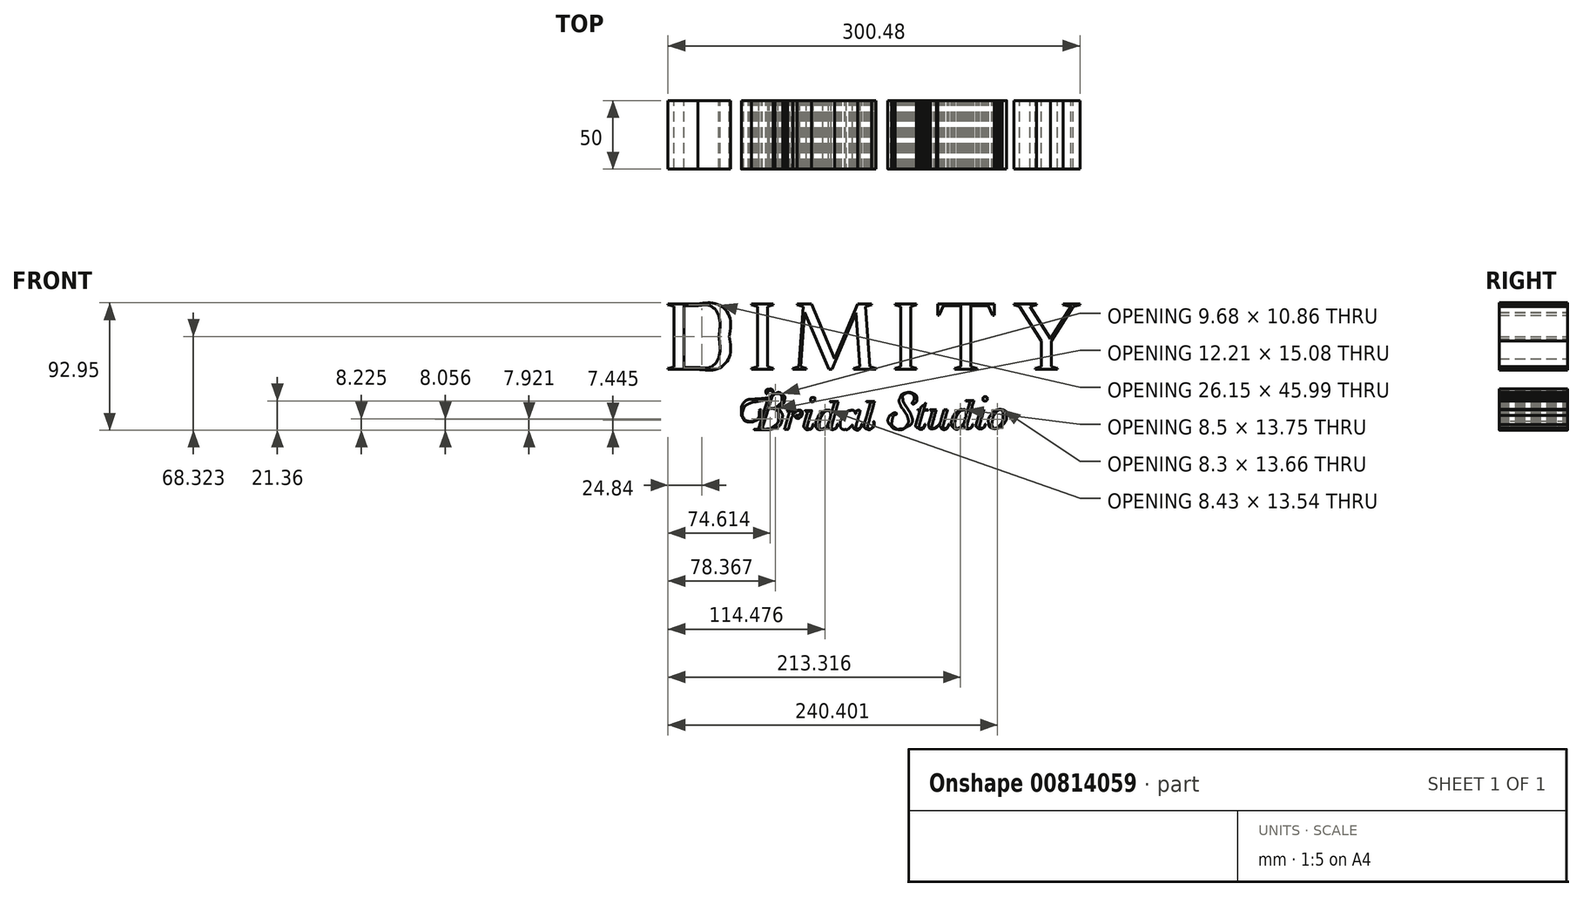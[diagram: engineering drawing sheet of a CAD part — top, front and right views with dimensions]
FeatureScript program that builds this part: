
annotation { "Feature Type Name" : "Feature", "Feature Type Description" : "" }
export const myFeature = defineFeature(function(context is Context, id is Id, definition is map)
    precondition{}
    {
        {
            var Q0;
            Q0=qCreatedBy(makeId("Front.planeOp"),FACE);
            var sketch = newSketch(context, id + "F0", { "sketchPlane" : qUnion([Q0])});
            skLineSegment(sketch, "E0", {"start": v(-150.24, 61.58) * mm, "end": v(-150.24, 60.97) * mm});
            skLineSegment(sketch, "E1", {"start": v(-150.24, 60.97) * mm, "end": v(-145.82, 59.95) * mm});
            skLineSegment(sketch, "E2", {"start": v(-145.82, 59.95) * mm, "end": v(-145.82, 15.6) * mm});
            skLineSegment(sketch, "E3", {"start": v(-145.82, 15.6) * mm, "end": v(-150.24, 14.5) * mm});
            skLineSegment(sketch, "E4", {"start": v(-150.24, 14.5) * mm, "end": v(-150.24, 13.96) * mm});
            skLineSegment(sketch, "E5", {"start": v(-150.24, 13.96) * mm, "end": v(-128.54, 13.96) * mm});
            skFitSpline(sketch, "E6", {"points": [v(-128.54, 13.96) * mm, v(-114.94, 13.96) * mm, v(-105.41, 22.8) * mm, v(-105.41, 37.77) * mm]});
            skFitSpline(sketch, "E7", {"points": [v(-105.41, 37.77) * mm, v(-105.41, 52.6) * mm, v(-114.94, 61.58) * mm, v(-128.54, 61.58) * mm]});
            skLineSegment(sketch, "E8", {"start": v(-128.54, 61.58) * mm, "end": v(-150.24, 61.58) * mm});
            skLineSegment(sketch, "E9", {"start": v(-138.48, 60.22) * mm, "end": v(-128.54, 60.22) * mm});
            skFitSpline(sketch, "E10", {"points": [v(-128.54, 60.22) * mm, v(-119.56, 60.22) * mm, v(-113.1, 52.74) * mm, v(-113.1, 37.7) * mm]});
            skFitSpline(sketch, "E11", {"points": [v(-113.1, 37.7) * mm, v(-113.1, 22.74) * mm, v(-119.56, 15.32) * mm, v(-128.54, 15.32) * mm]});
            skLineSegment(sketch, "E12", {"start": v(-128.54, 15.32) * mm, "end": v(-138.48, 15.32) * mm});
            skLineSegment(sketch, "E13", {"start": v(-138.48, 15.32) * mm, "end": v(-138.48, 60.22) * mm});
            skLineSegment(sketch, "E14", {"start": v(-89.22, 61.58) * mm, "end": v(-89.22, 60.9) * mm});
            skLineSegment(sketch, "E15", {"start": v(-89.22, 60.9) * mm, "end": v(-84.8, 59.6) * mm});
            skLineSegment(sketch, "E16", {"start": v(-84.8, 59.6) * mm, "end": v(-84.8, 15.93) * mm});
            skLineSegment(sketch, "E17", {"start": v(-84.8, 15.93) * mm, "end": v(-89.22, 14.64) * mm});
            skLineSegment(sketch, "E18", {"start": v(-89.22, 14.64) * mm, "end": v(-89.22, 13.96) * mm});
            skLineSegment(sketch, "E19", {"start": v(-89.22, 13.96) * mm, "end": v(-73.37, 13.96) * mm});
            skLineSegment(sketch, "E20", {"start": v(-73.37, 13.96) * mm, "end": v(-73.37, 14.64) * mm});
            skLineSegment(sketch, "E21", {"start": v(-73.37, 14.64) * mm, "end": v(-77.59, 15.93) * mm});
            skLineSegment(sketch, "E22", {"start": v(-77.59, 15.93) * mm, "end": v(-77.59, 59.6) * mm});
            skLineSegment(sketch, "E23", {"start": v(-77.59, 59.6) * mm, "end": v(-73.37, 60.9) * mm});
            skLineSegment(sketch, "E24", {"start": v(-73.37, 60.9) * mm, "end": v(-73.37, 61.58) * mm});
            skLineSegment(sketch, "E25", {"start": v(-73.37, 61.58) * mm, "end": v(-89.22, 61.58) * mm});
            skLineSegment(sketch, "E26", {"start": v(-56.1, 61.58) * mm, "end": v(-56.1, 60.9) * mm});
            skLineSegment(sketch, "E27", {"start": v(-56.1, 60.9) * mm, "end": v(-51.67, 59.6) * mm});
            skLineSegment(sketch, "E28", {"start": v(-51.67, 59.6) * mm, "end": v(-54.87, 15.8) * mm});
            skLineSegment(sketch, "E29", {"start": v(-54.87, 15.8) * mm, "end": v(-59.29, 14.5) * mm});
            skLineSegment(sketch, "E30", {"start": v(-59.29, 14.5) * mm, "end": v(-59.29, 13.96) * mm});
            skLineSegment(sketch, "E31", {"start": v(-59.29, 13.96) * mm, "end": v(-49.29, 13.96) * mm});
            skLineSegment(sketch, "E32", {"start": v(-49.29, 13.96) * mm, "end": v(-49.29, 14.5) * mm});
            skLineSegment(sketch, "E33", {"start": v(-49.29, 14.5) * mm, "end": v(-53.44, 15.8) * mm});
            skLineSegment(sketch, "E34", {"start": v(-53.44, 15.8) * mm, "end": v(-50.51, 55.4) * mm});
            skLineSegment(sketch, "E35", {"start": v(-50.51, 55.4) * mm, "end": v(-32.76, 13.96) * mm});
            skLineSegment(sketch, "E36", {"start": v(-32.76, 13.96) * mm, "end": v(-30.51, 13.96) * mm});
            skLineSegment(sketch, "E37", {"start": v(-30.51, 13.96) * mm, "end": v(-13.03, 55.32) * mm});
            skLineSegment(sketch, "E38", {"start": v(-13.03, 55.32) * mm, "end": v(-10.17, 15.93) * mm});
            skLineSegment(sketch, "E39", {"start": v(-10.17, 15.93) * mm, "end": v(-14.6, 14.64) * mm});
            skLineSegment(sketch, "E40", {"start": v(-14.6, 14.64) * mm, "end": v(-14.6, 13.96) * mm});
            skLineSegment(sketch, "E41", {"start": v(-14.6, 13.96) * mm, "end": v(1.32, 13.96) * mm});
            skLineSegment(sketch, "E42", {"start": v(1.32, 13.96) * mm, "end": v(1.32, 14.64) * mm});
            skLineSegment(sketch, "E43", {"start": v(1.32, 14.64) * mm, "end": v(-2.9, 15.93) * mm});
            skLineSegment(sketch, "E44", {"start": v(-2.9, 15.93) * mm, "end": v(-6.02, 59.6) * mm});
            skLineSegment(sketch, "E45", {"start": v(-6.02, 59.6) * mm, "end": v(-1.8, 60.9) * mm});
            skLineSegment(sketch, "E46", {"start": v(-1.8, 60.9) * mm, "end": v(-1.8, 61.58) * mm});
            skLineSegment(sketch, "E47", {"start": v(-1.8, 61.58) * mm, "end": v(-11.8, 61.58) * mm});
            skLineSegment(sketch, "E48", {"start": v(-11.8, 61.58) * mm, "end": v(-28.68, 21.44) * mm});
            skLineSegment(sketch, "E49", {"start": v(-28.68, 21.44) * mm, "end": v(-45.68, 61.58) * mm});
            skLineSegment(sketch, "E50", {"start": v(-45.68, 61.58) * mm, "end": v(-56.1, 61.58) * mm});
            skLineSegment(sketch, "E51", {"start": v(15.27, 61.58) * mm, "end": v(15.27, 60.9) * mm});
            skLineSegment(sketch, "E52", {"start": v(15.27, 60.9) * mm, "end": v(19.7, 59.6) * mm});
            skLineSegment(sketch, "E53", {"start": v(19.7, 59.6) * mm, "end": v(19.7, 15.93) * mm});
            skLineSegment(sketch, "E54", {"start": v(19.7, 15.93) * mm, "end": v(15.27, 14.64) * mm});
            skLineSegment(sketch, "E55", {"start": v(15.27, 14.64) * mm, "end": v(15.27, 13.96) * mm});
            skLineSegment(sketch, "E56", {"start": v(15.27, 13.96) * mm, "end": v(31.12, 13.96) * mm});
            skLineSegment(sketch, "E57", {"start": v(31.12, 13.96) * mm, "end": v(31.12, 14.64) * mm});
            skLineSegment(sketch, "E58", {"start": v(31.12, 14.64) * mm, "end": v(26.9, 15.93) * mm});
            skLineSegment(sketch, "E59", {"start": v(26.9, 15.93) * mm, "end": v(26.9, 59.6) * mm});
            skLineSegment(sketch, "E60", {"start": v(26.9, 59.6) * mm, "end": v(31.12, 60.9) * mm});
            skLineSegment(sketch, "E61", {"start": v(31.12, 60.9) * mm, "end": v(31.12, 61.58) * mm});
            skLineSegment(sketch, "E62", {"start": v(31.12, 61.58) * mm, "end": v(15.27, 61.58) * mm});
            skLineSegment(sketch, "E63", {"start": v(46.5, 61.58) * mm, "end": v(46.5, 53.21) * mm});
            skLineSegment(sketch, "E64", {"start": v(46.5, 53.21) * mm, "end": v(47.59, 53.21) * mm});
            skLineSegment(sketch, "E65", {"start": v(47.59, 53.21) * mm, "end": v(50.79, 60.22) * mm});
            skLineSegment(sketch, "E66", {"start": v(50.79, 60.22) * mm, "end": v(63.44, 60.22) * mm});
            skLineSegment(sketch, "E67", {"start": v(63.44, 60.22) * mm, "end": v(63.44, 15.93) * mm});
            skLineSegment(sketch, "E68", {"start": v(63.44, 15.93) * mm, "end": v(59.02, 14.64) * mm});
            skLineSegment(sketch, "E69", {"start": v(59.02, 14.64) * mm, "end": v(59.02, 13.96) * mm});
            skLineSegment(sketch, "E70", {"start": v(59.02, 13.96) * mm, "end": v(75.2, 13.96) * mm});
            skLineSegment(sketch, "E71", {"start": v(75.2, 13.96) * mm, "end": v(75.2, 14.64) * mm});
            skLineSegment(sketch, "E72", {"start": v(75.2, 14.64) * mm, "end": v(70.79, 15.93) * mm});
            skLineSegment(sketch, "E73", {"start": v(70.79, 15.93) * mm, "end": v(70.79, 60.22) * mm});
            skLineSegment(sketch, "E74", {"start": v(70.79, 60.22) * mm, "end": v(83.5, 60.22) * mm});
            skLineSegment(sketch, "E75", {"start": v(83.5, 60.22) * mm, "end": v(86.64, 53.21) * mm});
            skLineSegment(sketch, "E76", {"start": v(86.64, 53.21) * mm, "end": v(87.8, 53.21) * mm});
            skLineSegment(sketch, "E77", {"start": v(87.8, 53.21) * mm, "end": v(87.8, 61.58) * mm});
            skLineSegment(sketch, "E78", {"start": v(87.8, 61.58) * mm, "end": v(46.5, 61.58) * mm});
            skLineSegment(sketch, "E79", {"start": v(102.08, 61.58) * mm, "end": v(102.08, 60.9) * mm});
            skLineSegment(sketch, "E80", {"start": v(102.08, 60.9) * mm, "end": v(106.3, 59.6) * mm});
            skLineSegment(sketch, "E81", {"start": v(106.3, 59.6) * mm, "end": v(122.22, 34.64) * mm});
            skLineSegment(sketch, "E82", {"start": v(122.22, 34.64) * mm, "end": v(122.22, 15.93) * mm});
            skLineSegment(sketch, "E83", {"start": v(122.22, 15.93) * mm, "end": v(117.8, 14.64) * mm});
            skLineSegment(sketch, "E84", {"start": v(117.8, 14.64) * mm, "end": v(117.8, 13.96) * mm});
            skLineSegment(sketch, "E85", {"start": v(117.8, 13.96) * mm, "end": v(133.71, 13.96) * mm});
            skLineSegment(sketch, "E86", {"start": v(133.71, 13.96) * mm, "end": v(133.71, 14.64) * mm});
            skLineSegment(sketch, "E87", {"start": v(133.71, 14.64) * mm, "end": v(129.5, 15.93) * mm});
            skLineSegment(sketch, "E88", {"start": v(129.5, 15.93) * mm, "end": v(129.5, 34.64) * mm});
            skLineSegment(sketch, "E89", {"start": v(129.5, 34.64) * mm, "end": v(145.41, 59.6) * mm});
            skLineSegment(sketch, "E90", {"start": v(145.41, 59.6) * mm, "end": v(150.24, 60.9) * mm});
            skLineSegment(sketch, "E91", {"start": v(150.24, 60.9) * mm, "end": v(150.24, 61.58) * mm});
            skLineSegment(sketch, "E92", {"start": v(150.24, 61.58) * mm, "end": v(138.14, 61.58) * mm});
            skLineSegment(sketch, "E93", {"start": v(138.14, 61.58) * mm, "end": v(138.14, 60.9) * mm});
            skLineSegment(sketch, "E94", {"start": v(138.14, 60.9) * mm, "end": v(143.85, 59.6) * mm});
            skLineSegment(sketch, "E95", {"start": v(143.85, 59.6) * mm, "end": v(128.82, 36.14) * mm});
            skLineSegment(sketch, "E96", {"start": v(128.82, 36.14) * mm, "end": v(113.99, 59.6) * mm});
            skLineSegment(sketch, "E97", {"start": v(113.99, 59.6) * mm, "end": v(118.48, 60.9) * mm});
            skLineSegment(sketch, "E98", {"start": v(118.48, 60.9) * mm, "end": v(118.48, 61.58) * mm});
            skLineSegment(sketch, "E99", {"start": v(118.48, 61.58) * mm, "end": v(102.08, 61.58) * mm});
            skFitSpline(sketch, "E100", {"points": [v(-76.4, -0.67) * mm, v(-76.52, -0.68) * mm, v(-76.64, -0.69) * mm, v(-76.77, -0.7) * mm]});
            skFitSpline(sketch, "E101", {"points": [v(-76.77, -0.7) * mm, v(-78.1, -0.88) * mm, v(-78.95, -2.12) * mm, v(-78.66, -3.42) * mm]});
            skFitSpline(sketch, "E102", {"points": [v(-78.66, -3.42) * mm, v(-78.58, -3.77) * mm, v(-78.42, -4.03) * mm, v(-78.01, -4.17) * mm]});
            skFitSpline(sketch, "E103", {"points": [v(-78.01, -4.17) * mm, v(-77.88, -3.84) * mm, v(-77.75, -3.53) * mm, v(-77.63, -3.23) * mm]});
            skFitSpline(sketch, "E104", {"points": [v(-77.63, -3.23) * mm, v(-77.3, -2.4) * mm, v(-76.7, -1.9) * mm, v(-75.86, -1.7) * mm]});
            skFitSpline(sketch, "E105", {"points": [v(-75.86, -1.7) * mm, v(-75.1, -1.5) * mm, v(-74.23, -1.76) * mm, v(-73.8, -2.9) * mm]});
            skFitSpline(sketch, "E106", {"points": [v(-73.8, -2.9) * mm, v(-73.64, -3.48) * mm, v(-73.71, -3.7) * mm, v(-73.8, -3.99) * mm]});
            skFitSpline(sketch, "E107", {"points": [v(-73.8, -3.99) * mm, v(-74.16, -4.85) * mm, v(-74.64, -5.5) * mm, v(-75.38, -5.97) * mm]});
            skFitSpline(sketch, "E108", {"points": [v(-75.38, -5.97) * mm, v(-76.37, -6.6) * mm, v(-77.46, -6.98) * mm, v(-78.6, -7.13) * mm]});
            skFitSpline(sketch, "E109", {"points": [v(-78.6, -7.13) * mm, v(-80.37, -7.36) * mm, v(-82.16, -7.53) * mm, v(-83.95, -7.6) * mm]});
            skFitSpline(sketch, "E110", {"points": [v(-83.95, -7.6) * mm, v(-85.37, -7.64) * mm, v(-86.76, -7.81) * mm, v(-88.16, -8) * mm]});
            skFitSpline(sketch, "E111", {"points": [v(-88.16, -8) * mm, v(-92.67, -8.6) * mm, v(-96.35, -12.56) * mm, v(-96.65, -16.82) * mm]});
            skFitSpline(sketch, "E112", {"points": [v(-96.65, -16.82) * mm, v(-96.76, -18.4) * mm, v(-96.57, -19.87) * mm, v(-95.83, -21.26) * mm]});
            skFitSpline(sketch, "E113", {"points": [v(-95.83, -21.26) * mm, v(-94.76, -23.27) * mm, v(-93.03, -24.27) * mm, v(-90.8, -24.44) * mm]});
            skFitSpline(sketch, "E114", {"points": [v(-90.8, -24.44) * mm, v(-89.36, -24.54) * mm, v(-87.99, -24.3) * mm, v(-86.66, -23.74) * mm]});
            skFitSpline(sketch, "E115", {"points": [v(-86.66, -23.74) * mm, v(-84.6, -22.87) * mm, v(-82.99, -21.52) * mm, v(-82.1, -19.41) * mm]});
            skFitSpline(sketch, "E116", {"points": [v(-82.1, -19.41) * mm, v(-81.75, -18.57) * mm, v(-81.63, -17.7) * mm, v(-81.92, -16.82) * mm]});
            skFitSpline(sketch, "E117", {"points": [v(-81.92, -16.82) * mm, v(-82.23, -15.91) * mm, v(-83.02, -15.66) * mm, v(-83.94, -16.22) * mm]});
            skFitSpline(sketch, "E118", {"points": [v(-83.94, -16.22) * mm, v(-83.56, -16.94) * mm, v(-83.62, -17.7) * mm, v(-83.68, -18.42) * mm]});
            skFitSpline(sketch, "E119", {"points": [v(-83.68, -18.42) * mm, v(-83.88, -20.82) * mm, v(-85.05, -22.56) * mm, v(-87.27, -23.54) * mm]});
            skFitSpline(sketch, "E120", {"points": [v(-87.27, -23.54) * mm, v(-88.7, -24.17) * mm, v(-90.18, -24.3) * mm, v(-91.7, -23.95) * mm]});
            skFitSpline(sketch, "E121", {"points": [v(-91.7, -23.95) * mm, v(-93.1, -23.63) * mm, v(-94.26, -22.9) * mm, v(-94.99, -21.61) * mm]});
            skFitSpline(sketch, "E122", {"points": [v(-94.99, -21.61) * mm, v(-95.98, -19.85) * mm, v(-96.04, -17.97) * mm, v(-95.36, -16.13) * mm]});
            skFitSpline(sketch, "E123", {"points": [v(-95.36, -16.13) * mm, v(-94.4, -13.55) * mm, v(-92.5, -11.84) * mm, v(-89.98, -10.77) * mm]});
            skFitSpline(sketch, "E124", {"points": [v(-89.98, -10.77) * mm, v(-88.26, -10.04) * mm, v(-86.4, -9.88) * mm, v(-84.6, -9.53) * mm]});
            skFitSpline(sketch, "E125", {"points": [v(-84.6, -9.53) * mm, v(-82.4, -9.1) * mm, v(-80.2, -8.66) * mm, v(-78.1, -7.82) * mm]});
            skFitSpline(sketch, "E126", {"points": [v(-78.1, -7.82) * mm, v(-77.9, -7.74) * mm, v(-77.67, -7.7) * mm, v(-77.37, -7.61) * mm]});
            skFitSpline(sketch, "E127", {"points": [v(-77.37, -7.61) * mm, v(-79.72, -15.08) * mm, v(-82.04, -22.44) * mm, v(-84.39, -29.86) * mm]});
            skFitSpline(sketch, "E128", {"points": [v(-84.39, -29.86) * mm, v(-84.9, -29.86) * mm, v(-85.4, -29.84) * mm, v(-85.9, -29.87) * mm]});
            skFitSpline(sketch, "E129", {"points": [v(-85.9, -29.87) * mm, v(-86.39, -29.9) * mm, v(-86.9, -29.73) * mm, v(-87.35, -30.07) * mm]});
            skFitSpline(sketch, "E130", {"points": [v(-87.35, -30.07) * mm, v(-87.1, -30.16) * mm, v(-86.84, -30.18) * mm, v(-86.58, -30.19) * mm]});
            skFitSpline(sketch, "E131", {"points": [v(-86.58, -30.19) * mm, v(-83.85, -30.19) * mm, v(-81.12, -30.18) * mm, v(-78.4, -30.19) * mm]});
            skFitSpline(sketch, "E132", {"points": [v(-78.4, -30.19) * mm, v(-77.22, -30.2) * mm, v(-76.05, -30.1) * mm, v(-74.92, -29.76) * mm]});
            skFitSpline(sketch, "E133", {"points": [v(-74.92, -29.76) * mm, v(-70.73, -28.54) * mm, v(-67.89, -25.98) * mm, v(-66.95, -21.6) * mm]});
            skFitSpline(sketch, "E134", {"points": [v(-66.95, -21.6) * mm, v(-66.64, -20.14) * mm, v(-66.88, -18.71) * mm, v(-67.65, -17.44) * mm]});
            skFitSpline(sketch, "E135", {"points": [v(-67.65, -17.44) * mm, v(-68.51, -16.03) * mm, v(-69.82, -15.18) * mm, v(-71.42, -14.78) * mm]});
            skFitSpline(sketch, "E136", {"points": [v(-71.42, -14.78) * mm, v(-71.73, -14.7) * mm, v(-72.03, -14.64) * mm, v(-72.33, -14.57) * mm]});
            skFitSpline(sketch, "E137", {"points": [v(-72.33, -14.57) * mm, v(-70.94, -14.15) * mm, v(-69.63, -13.66) * mm, v(-68.44, -12.87) * mm]});
            skFitSpline(sketch, "E138", {"points": [v(-68.44, -12.87) * mm, v(-66.76, -11.76) * mm, v(-65.52, -10.32) * mm, v(-65.19, -8.27) * mm]});
            skFitSpline(sketch, "E139", {"points": [v(-65.19, -8.27) * mm, v(-64.95, -6.76) * mm, v(-65.39, -5.42) * mm, v(-66.64, -4.52) * mm]});
            skFitSpline(sketch, "E140", {"points": [v(-66.64, -4.52) * mm, v(-68.4, -3.25) * mm, v(-70.34, -3.07) * mm, v(-72.33, -4.03) * mm]});
            skFitSpline(sketch, "E141", {"points": [v(-72.33, -4.03) * mm, v(-72.77, -4.24) * mm, v(-73.2, -4.48) * mm, v(-73.74, -4.77) * mm]});
            skFitSpline(sketch, "E142", {"points": [v(-73.74, -4.77) * mm, v(-73.64, -4.31) * mm, v(-73.5, -3.97) * mm, v(-73.51, -3.63) * mm]});
            skFitSpline(sketch, "E143", {"points": [v(-73.51, -3.63) * mm, v(-73.55, -1.93) * mm, v(-74.62, -0.6) * mm, v(-76.4, -0.67) * mm]});
            skFitSpline(sketch, "E144", {"points": [v(-70.2, -3.8) * mm, v(-69.3, -3.77) * mm, v(-68.48, -4.04) * mm, v(-67.89, -4.82) * mm]});
            skFitSpline(sketch, "E145", {"points": [v(-67.89, -4.82) * mm, v(-67.46, -5.37) * mm, v(-67.2, -6.01) * mm, v(-67.17, -6.73) * mm]});
            skFitSpline(sketch, "E146", {"points": [v(-67.17, -6.73) * mm, v(-67.1, -9.1) * mm, v(-68.09, -11.01) * mm, v(-69.86, -12.5) * mm]});
            skFitSpline(sketch, "E147", {"points": [v(-69.86, -12.5) * mm, v(-71.8, -14.12) * mm, v(-74.09, -14.63) * mm, v(-76.56, -14.46) * mm]});
            skFitSpline(sketch, "E148", {"points": [v(-76.56, -14.46) * mm, v(-76.6, -14.46) * mm, v(-76.65, -14.42) * mm, v(-76.69, -14.4) * mm]});
            skFitSpline(sketch, "E149", {"points": [v(-76.69, -14.4) * mm, v(-76.7, -13.96) * mm, v(-74.67, -7.33) * mm, v(-73.93, -5.43) * mm]});
            skFitSpline(sketch, "E150", {"points": [v(-73.93, -5.43) * mm, v(-72.96, -4.66) * mm, v(-71.88, -3.98) * mm, v(-70.58, -3.83) * mm]});
            skFitSpline(sketch, "E151", {"points": [v(-70.58, -3.83) * mm, v(-70.45, -3.81) * mm, v(-70.32, -3.8) * mm, v(-70.2, -3.8) * mm]});
            skFitSpline(sketch, "E152", {"points": [v(-76.94, -14.8) * mm, v(-75.98, -14.8) * mm, v(-75.14, -14.78) * mm, v(-74.3, -14.8) * mm]});
            skFitSpline(sketch, "E153", {"points": [v(-74.3, -14.8) * mm, v(-73.48, -14.8) * mm, v(-72.68, -14.98) * mm, v(-71.97, -15.4) * mm]});
            skFitSpline(sketch, "E154", {"points": [v(-71.97, -15.4) * mm, v(-70.52, -16.27) * mm, v(-69.8, -17.62) * mm, v(-69.75, -19.27) * mm]});
            skFitSpline(sketch, "E155", {"points": [v(-69.75, -19.27) * mm, v(-69.64, -23.38) * mm, v(-71.38, -26.56) * mm, v(-74.84, -28.76) * mm]});
            skFitSpline(sketch, "E156", {"points": [v(-74.84, -28.76) * mm, v(-75.74, -29.33) * mm, v(-76.75, -29.65) * mm, v(-77.81, -29.73) * mm]});
            skFitSpline(sketch, "E157", {"points": [v(-77.81, -29.73) * mm, v(-78.98, -29.81) * mm, v(-80.15, -29.82) * mm, v(-81.32, -29.86) * mm]});
            skFitSpline(sketch, "E158", {"points": [v(-81.32, -29.86) * mm, v(-81.44, -29.86) * mm, v(-81.55, -29.84) * mm, v(-81.73, -29.82) * mm]});
            skFitSpline(sketch, "E159", {"points": [v(-81.73, -29.82) * mm, v(-80.12, -24.78) * mm, v(-78.53, -19.78) * mm, v(-76.94, -14.8) * mm]});
            skFitSpline(sketch, "E160", {"points": [v(-49.72, -16.11) * mm, v(-49.94, -16.11) * mm, v(-50.14, -16.17) * mm, v(-50.25, -16.53) * mm]});
            skLineSegment(sketch, "E161", {"start": v(-50.25, -16.53) * mm, "end": v(-46.95, -16.53) * mm});
            skFitSpline(sketch, "E162", {"points": [v(-46.95, -16.53) * mm, v(-47.84, -16.92) * mm, v(-48.43, -17.53) * mm, v(-48.74, -18.42) * mm]});
            skFitSpline(sketch, "E163", {"points": [v(-48.74, -18.42) * mm, v(-48.85, -18.71) * mm, v(-48.95, -19) * mm, v(-49.04, -19.3) * mm]});
            skFitSpline(sketch, "E164", {"points": [v(-49.04, -19.3) * mm, v(-49.43, -20.65) * mm, v(-49.82, -22) * mm, v(-50.2, -23.36) * mm]});
            skFitSpline(sketch, "E165", {"points": [v(-50.2, -23.36) * mm, v(-50.51, -24.44) * mm, v(-50.84, -25.52) * mm, v(-51.13, -26.6) * mm]});
            skFitSpline(sketch, "E166", {"points": [v(-51.13, -26.6) * mm, v(-51.33, -27.38) * mm, v(-51.23, -28.14) * mm, v(-50.68, -28.76) * mm]});
            skFitSpline(sketch, "E167", {"points": [v(-50.68, -28.76) * mm, v(-49.74, -29.85) * mm, v(-48.5, -30.2) * mm, v(-47.12, -29.9) * mm]});
            skFitSpline(sketch, "E168", {"points": [v(-47.12, -29.9) * mm, v(-45.7, -29.6) * mm, v(-44.94, -28.54) * mm, v(-44.42, -27.27) * mm]});
            skFitSpline(sketch, "E169", {"points": [v(-44.42, -27.27) * mm, v(-44.28, -26.9) * mm, v(-44.22, -26.51) * mm, v(-44.1, -26) * mm]});
            skFitSpline(sketch, "E170", {"points": [v(-44.1, -26) * mm, v(-44.53, -26.36) * mm, v(-44.5, -26.36) * mm, v(-44.6, -26.73) * mm]});
            skFitSpline(sketch, "E171", {"points": [v(-44.6, -26.73) * mm, v(-45.01, -28.1) * mm, v(-45.71, -29.2) * mm, v(-47.22, -29.6) * mm]});
            skFitSpline(sketch, "E172", {"points": [v(-47.22, -29.6) * mm, v(-48.17, -29.84) * mm, v(-48.76, -29.45) * mm, v(-48.73, -28.48) * mm]});
            skFitSpline(sketch, "E173", {"points": [v(-48.73, -28.48) * mm, v(-48.7, -27.82) * mm, v(-48.57, -27.15) * mm, v(-48.4, -26.5) * mm]});
            skFitSpline(sketch, "E174", {"points": [v(-48.4, -26.5) * mm, v(-48.04, -25.17) * mm, v(-47.62, -23.85) * mm, v(-47.24, -22.52) * mm]});
            skFitSpline(sketch, "E175", {"points": [v(-47.24, -22.52) * mm, v(-46.7, -20.66) * mm, v(-45.37, -16.14) * mm, v(-45.41, -16.14) * mm]});
            skFitSpline(sketch, "E176", {"points": [v(-45.41, -16.14) * mm, v(-46.73, -16.13) * mm, v(-48.4, -16.12) * mm, v(-49.72, -16.11) * mm]});
            skFitSpline(sketch, "E177", {"points": [v(-44.59, -6.73) * mm, v(-45.46, -6.76) * mm, v(-46.22, -7.78) * mm, v(-46.2, -8.44) * mm]});
            skFitSpline(sketch, "E178", {"points": [v(-46.2, -8.44) * mm, v(-46.16, -9.31) * mm, v(-45.35, -9.95) * mm, v(-44.51, -9.72) * mm]});
            skFitSpline(sketch, "E179", {"points": [v(-44.51, -9.72) * mm, v(-43.93, -9.55) * mm, v(-43.48, -9.18) * mm, v(-43.26, -8.62) * mm]});
            skFitSpline(sketch, "E180", {"points": [v(-43.26, -8.62) * mm, v(-42.83, -7.55) * mm, v(-43.6, -6.64) * mm, v(-44.41, -6.73) * mm]});
            skFitSpline(sketch, "E181", {"points": [v(-44.41, -6.73) * mm, v(-44.47, -6.73) * mm, v(-44.53, -6.72) * mm, v(-44.59, -6.73) * mm]});
            skFitSpline(sketch, "E182", {"points": [v(-54.55, -16.02) * mm, v(-55.27, -16) * mm, v(-55.94, -16.19) * mm, v(-56.57, -16.56) * mm]});
            skFitSpline(sketch, "E183", {"points": [v(-56.57, -16.56) * mm, v(-57.8, -17.3) * mm, v(-58.69, -18.34) * mm, v(-59.55, -19.5) * mm]});
            skFitSpline(sketch, "E184", {"points": [v(-59.55, -19.5) * mm, v(-59.25, -18.41) * mm, v(-58.95, -17.32) * mm, v(-58.63, -16.15) * mm]});
            skFitSpline(sketch, "E185", {"points": [v(-58.63, -16.15) * mm, v(-58.99, -16.13) * mm, v(-62.49, -16.1) * mm, v(-62.95, -16.1) * mm]});
            skFitSpline(sketch, "E186", {"points": [v(-62.95, -16.1) * mm, v(-63.17, -16.1) * mm, v(-63.38, -16.16) * mm, v(-63.49, -16.52) * mm]});
            skFitSpline(sketch, "E187", {"points": [v(-63.49, -16.52) * mm, v(-63.43, -16.52) * mm, v(-61.3, -16.52) * mm, v(-60.3, -16.52) * mm]});
            skFitSpline(sketch, "E188", {"points": [v(-60.3, -16.52) * mm, v(-61.35, -17.07) * mm, v(-61.85, -17.95) * mm, v(-62.15, -19.01) * mm]});
            skFitSpline(sketch, "E189", {"points": [v(-62.15, -19.01) * mm, v(-62.95, -21.86) * mm, v(-63.77, -24.71) * mm, v(-64.58, -27.56) * mm]});
            skFitSpline(sketch, "E190", {"points": [v(-64.58, -27.56) * mm, v(-64.79, -28.29) * mm, v(-64.98, -29.02) * mm, v(-65.18, -29.74) * mm]});
            skFitSpline(sketch, "E191", {"points": [v(-65.18, -29.74) * mm, v(-64.54, -29.97) * mm, v(-63.1, -29.97) * mm, v(-62.5, -29.76) * mm]});
            skFitSpline(sketch, "E192", {"points": [v(-62.5, -29.76) * mm, v(-62.45, -29.65) * mm, v(-62.4, -29.52) * mm, v(-62.35, -29.38) * mm]});
            skFitSpline(sketch, "E193", {"points": [v(-62.35, -29.38) * mm, v(-61.93, -27.94) * mm, v(-61.52, -26.5) * mm, v(-61.1, -25.05) * mm]});
            skFitSpline(sketch, "E194", {"points": [v(-61.1, -25.05) * mm, v(-60.66, -23.54) * mm, v(-60.3, -22) * mm, v(-59.58, -20.58) * mm]});
            skFitSpline(sketch, "E195", {"points": [v(-59.58, -20.58) * mm, v(-58.94, -19.32) * mm, v(-58.14, -18.21) * mm, v(-57.05, -17.31) * mm]});
            skFitSpline(sketch, "E196", {"points": [v(-57.05, -17.31) * mm, v(-56.28, -16.67) * mm, v(-55.39, -16.29) * mm, v(-54.34, -16.39) * mm]});
            skFitSpline(sketch, "E197", {"points": [v(-54.34, -16.39) * mm, v(-53.87, -16.43) * mm, v(-53.61, -16.59) * mm, v(-53.54, -16.96) * mm]});
            skFitSpline(sketch, "E198", {"points": [v(-53.54, -16.96) * mm, v(-53.44, -17.41) * mm, v(-53.44, -17.87) * mm, v(-53.69, -18.28) * mm]});
            skFitSpline(sketch, "E199", {"points": [v(-53.69, -18.28) * mm, v(-54.26, -19.26) * mm, v(-55.09, -19.83) * mm, v(-56.25, -19.84) * mm]});
            skFitSpline(sketch, "E200", {"points": [v(-56.25, -19.84) * mm, v(-56.53, -19.84) * mm, v(-56.81, -19.84) * mm, v(-57.06, -19.84) * mm]});
            skFitSpline(sketch, "E201", {"points": [v(-57.06, -19.84) * mm, v(-57.33, -20.72) * mm, v(-56.98, -21.46) * mm, v(-56.23, -21.7) * mm]});
            skFitSpline(sketch, "E202", {"points": [v(-56.23, -21.7) * mm, v(-55.27, -22) * mm, v(-54.42, -21.7) * mm, v(-53.7, -21.1) * mm]});
            skFitSpline(sketch, "E203", {"points": [v(-53.7, -21.1) * mm, v(-52.78, -20.32) * mm, v(-52.38, -19.27) * mm, v(-52.37, -18.1) * mm]});
            skFitSpline(sketch, "E204", {"points": [v(-52.37, -18.1) * mm, v(-52.35, -16.98) * mm, v(-53.11, -16.18) * mm, v(-54.24, -16.05) * mm]});
            skFitSpline(sketch, "E205", {"points": [v(-54.24, -16.05) * mm, v(-54.35, -16.03) * mm, v(-54.45, -16.03) * mm, v(-54.55, -16.02) * mm]});
            skFitSpline(sketch, "E206", {"points": [v(-5.11, -9.56) * mm, v(-5.33, -9.56) * mm, v(-5.54, -9.61) * mm, v(-5.65, -9.97) * mm]});
            skLineSegment(sketch, "E207", {"start": v(-5.65, -9.97) * mm, "end": v(-2.05, -9.97) * mm});
            skFitSpline(sketch, "E208", {"points": [v(-2.05, -9.97) * mm, v(-1.98, -9.98) * mm, v(-1.92, -9.98) * mm, v(-1.85, -9.98) * mm]});
            skFitSpline(sketch, "E209", {"points": [v(-1.85, -9.98) * mm, v(-2.6, -10.82) * mm, v(-2.92, -11.82) * mm, v(-3.16, -12.84) * mm]});
            skFitSpline(sketch, "E210", {"points": [v(-3.16, -12.84) * mm, v(-3.2, -13) * mm, v(-3.24, -13.17) * mm, v(-3.29, -13.33) * mm]});
            skFitSpline(sketch, "E211", {"points": [v(-3.29, -13.33) * mm, v(-4.4, -17.16) * mm, v(-5.52, -20.99) * mm, v(-6.61, -24.83) * mm]});
            skFitSpline(sketch, "E212", {"points": [v(-6.61, -24.83) * mm, v(-6.85, -25.67) * mm, v(-7.19, -26.5) * mm, v(-7.13, -27.41) * mm]});
            skFitSpline(sketch, "E213", {"points": [v(-7.13, -27.41) * mm, v(-7.07, -28.3) * mm, v(-6.7, -28.98) * mm, v(-5.92, -29.4) * mm]});
            skFitSpline(sketch, "E214", {"points": [v(-5.92, -29.4) * mm, v(-5.49, -29.63) * mm, v(-5, -29.77) * mm, v(-4.52, -29.91) * mm]});
            skFitSpline(sketch, "E215", {"points": [v(-4.52, -29.91) * mm, v(-3.46, -30.23) * mm, v(-2.48, -29.94) * mm, v(-1.7, -29.26) * mm]});
            skFitSpline(sketch, "E216", {"points": [v(-1.7, -29.26) * mm, v(-0.31, -28.05) * mm, v(0.25, -26.46) * mm, v(0.08, -24.63) * mm]});
            skFitSpline(sketch, "E217", {"points": [v(0.08, -24.63) * mm, v(0.07, -24.47) * mm, v(-0.04, -24.32) * mm, v(-0.1, -24.17) * mm]});
            skFitSpline(sketch, "E218", {"points": [v(-0.1, -24.17) * mm, v(-0.15, -24.18) * mm, v(-0.2, -24.2) * mm, v(-0.25, -24.2) * mm]});
            skFitSpline(sketch, "E219", {"points": [v(-0.25, -24.2) * mm, v(-0.27, -24.3) * mm, v(-0.34, -24.42) * mm, v(-0.32, -24.51) * mm]});
            skFitSpline(sketch, "E220", {"points": [v(-0.32, -24.51) * mm, v(-0.02, -25.63) * mm, v(-0.35, -26.66) * mm, v(-0.84, -27.63) * mm]});
            skFitSpline(sketch, "E221", {"points": [v(-0.84, -27.63) * mm, v(-1.35, -28.65) * mm, v(-2.13, -29.4) * mm, v(-3.3, -29.65) * mm]});
            skFitSpline(sketch, "E222", {"points": [v(-3.3, -29.65) * mm, v(-4.03, -29.8) * mm, v(-4.6, -29.4) * mm, v(-4.65, -28.66) * mm]});
            skFitSpline(sketch, "E223", {"points": [v(-4.65, -28.66) * mm, v(-4.7, -28) * mm, v(-4.61, -27.34) * mm, v(-4.42, -26.68) * mm]});
            skFitSpline(sketch, "E224", {"points": [v(-4.42, -26.68) * mm, v(-3.6, -23.9) * mm, v(-2.82, -21.13) * mm, v(-2.02, -18.35) * mm]});
            skFitSpline(sketch, "E225", {"points": [v(-2.02, -18.35) * mm, v(-1.34, -15.99) * mm, v(0.45, -9.67) * mm, v(0.56, -9.57) * mm]});
            skFitSpline(sketch, "E226", {"points": [v(0.56, -9.57) * mm, v(-0.01, -9.57) * mm, v(-4.54, -9.56) * mm, v(-5.11, -9.56) * mm]});
            skFitSpline(sketch, "E227", {"points": [v(25.53, -3.04) * mm, v(24.9, -3.03) * mm, v(24.25, -3.11) * mm, v(23.6, -3.28) * mm]});
            skFitSpline(sketch, "E228", {"points": [v(23.6, -3.28) * mm, v(21.4, -3.82) * mm, v(19.8, -5.11) * mm, v(18.94, -7.26) * mm]});
            skFitSpline(sketch, "E229", {"points": [v(18.94, -7.26) * mm, v(18.26, -8.95) * mm, v(18.58, -10.55) * mm, v(19.3, -12.12) * mm]});
            skFitSpline(sketch, "E230", {"points": [v(19.3, -12.12) * mm, v(20.1, -13.84) * mm, v(21.24, -15.36) * mm, v(22.28, -16.93) * mm]});
            skFitSpline(sketch, "E231", {"points": [v(22.28, -16.93) * mm, v(23.19, -18.28) * mm, v(24.07, -19.66) * mm, v(24.54, -21.24) * mm]});
            skFitSpline(sketch, "E232", {"points": [v(24.54, -21.24) * mm, v(25.17, -23.35) * mm, v(24.98, -25.34) * mm, v(23.58, -27.14) * mm]});
            skFitSpline(sketch, "E233", {"points": [v(23.58, -27.14) * mm, v(21.68, -29.59) * mm, v(17.77, -30.15) * mm, v(15.2, -28.53) * mm]});
            skFitSpline(sketch, "E234", {"points": [v(15.2, -28.53) * mm, v(13.78, -27.63) * mm, v(13, -26.35) * mm, v(13.07, -24.64) * mm]});
            skFitSpline(sketch, "E235", {"points": [v(13.07, -24.64) * mm, v(13.09, -24.1) * mm, v(13.12, -23.53) * mm, v(13.26, -23) * mm]});
            skFitSpline(sketch, "E236", {"points": [v(13.26, -23) * mm, v(13.72, -21.26) * mm, v(14.5, -19.74) * mm, v(16.3, -18.99) * mm]});
            skFitSpline(sketch, "E237", {"points": [v(16.3, -18.99) * mm, v(16.4, -18.95) * mm, v(16.48, -18.86) * mm, v(16.57, -18.8) * mm]});
            skFitSpline(sketch, "E238", {"points": [v(16.57, -18.8) * mm, v(16.21, -18.07) * mm, v(15.68, -17.78) * mm, v(14.94, -17.93) * mm]});
            skFitSpline(sketch, "E239", {"points": [v(14.94, -17.93) * mm, v(14.18, -18.09) * mm, v(13.5, -18.43) * mm, v(12.93, -18.97) * mm]});
            skFitSpline(sketch, "E240", {"points": [v(12.93, -18.97) * mm, v(10.9, -20.85) * mm, v(10.25, -24.44) * mm, v(12.22, -26.93) * mm]});
            skFitSpline(sketch, "E241", {"points": [v(12.22, -26.93) * mm, v(14.01, -29.19) * mm, v(16.45, -29.86) * mm, v(19.18, -29.7) * mm]});
            skFitSpline(sketch, "E242", {"points": [v(19.18, -29.7) * mm, v(20.7, -29.63) * mm, v(22.14, -29.2) * mm, v(23.48, -28.44) * mm]});
            skFitSpline(sketch, "E243", {"points": [v(23.48, -28.44) * mm, v(26.77, -26.6) * mm, v(28.24, -23.61) * mm, v(27.11, -19.8) * mm]});
            skFitSpline(sketch, "E244", {"points": [v(27.11, -19.8) * mm, v(26.65, -18.24) * mm, v(25.85, -16.86) * mm, v(24.98, -15.5) * mm]});
            skFitSpline(sketch, "E245", {"points": [v(24.98, -15.5) * mm, v(24.04, -14.06) * mm, v(23.08, -12.64) * mm, v(22.18, -11.17) * mm]});
            skFitSpline(sketch, "E246", {"points": [v(22.18, -11.17) * mm, v(21.56, -10.17) * mm, v(21.12, -9.08) * mm, v(21.04, -7.88) * mm]});
            skFitSpline(sketch, "E247", {"points": [v(21.04, -7.88) * mm, v(20.93, -6.3) * mm, v(21.34, -4.9) * mm, v(22.8, -4.07) * mm]});
            skFitSpline(sketch, "E248", {"points": [v(22.8, -4.07) * mm, v(24.3, -3.21) * mm, v(25.9, -3.17) * mm, v(27.5, -3.81) * mm]});
            skFitSpline(sketch, "E249", {"points": [v(27.5, -3.81) * mm, v(28, -4.01) * mm, v(28.37, -4.39) * mm, v(28.62, -4.87) * mm]});
            skFitSpline(sketch, "E250", {"points": [v(28.62, -4.87) * mm, v(29.39, -6.37) * mm, v(29.33, -7.87) * mm, v(28.63, -9.36) * mm]});
            skFitSpline(sketch, "E251", {"points": [v(28.63, -9.36) * mm, v(28.38, -9.9) * mm, v(28, -10.36) * mm, v(27.68, -10.86) * mm]});
            skFitSpline(sketch, "E252", {"points": [v(27.68, -10.86) * mm, v(28.37, -11.43) * mm, v(29.02, -11.47) * mm, v(29.74, -10.9) * mm]});
            skFitSpline(sketch, "E253", {"points": [v(29.74, -10.9) * mm, v(30.98, -9.9) * mm, v(31.46, -8.54) * mm, v(31.23, -7) * mm]});
            skFitSpline(sketch, "E254", {"points": [v(31.23, -7) * mm, v(31, -5.46) * mm, v(30, -4.44) * mm, v(28.64, -3.77) * mm]});
            skFitSpline(sketch, "E255", {"points": [v(28.64, -3.77) * mm, v(27.63, -3.28) * mm, v(26.6, -3.04) * mm, v(25.53, -3.04) * mm]});
            skFitSpline(sketch, "E256", {"points": [v(91.75, -15.4) * mm, v(91.18, -15.42) * mm, v(90.62, -15.52) * mm, v(90.06, -15.69) * mm]});
            skFitSpline(sketch, "E257", {"points": [v(90.06, -15.69) * mm, v(88.3, -16.23) * mm, v(86.91, -17.28) * mm, v(85.82, -18.74) * mm]});
            skFitSpline(sketch, "E258", {"points": [v(85.82, -18.74) * mm, v(84.3, -20.76) * mm, v(83.44, -22.99) * mm, v(83.7, -25.56) * mm]});
            skFitSpline(sketch, "E259", {"points": [v(83.7, -25.56) * mm, v(83.87, -27.12) * mm, v(84.58, -28.36) * mm, v(86.06, -28.98) * mm]});
            skFitSpline(sketch, "E260", {"points": [v(86.06, -28.98) * mm, v(86.75, -29.28) * mm, v(87.53, -29.34) * mm, v(88.22, -29.5) * mm]});
            skFitSpline(sketch, "E261", {"points": [v(88.22, -29.5) * mm, v(88.97, -29.36) * mm, v(89.64, -29.29) * mm, v(90.27, -29.11) * mm]});
            skFitSpline(sketch, "E262", {"points": [v(90.27, -29.11) * mm, v(91.92, -28.65) * mm, v(93.23, -27.65) * mm, v(94.29, -26.34) * mm]});
            skFitSpline(sketch, "E263", {"points": [v(94.29, -26.34) * mm, v(95.84, -24.43) * mm, v(96.76, -22.26) * mm, v(96.68, -19.74) * mm]});
            skFitSpline(sketch, "E264", {"points": [v(96.68, -19.74) * mm, v(96.6, -17.63) * mm, v(95.36, -16.05) * mm, v(93.46, -15.58) * mm]});
            skFitSpline(sketch, "E265", {"points": [v(93.46, -15.58) * mm, v(92.89, -15.44) * mm, v(92.32, -15.38) * mm, v(91.75, -15.4) * mm]});
            skFitSpline(sketch, "E266", {"points": [v(91.96, -15.68) * mm, v(92.05, -15.68) * mm, v(92.14, -15.69) * mm, v(92.23, -15.7) * mm]});
            skFitSpline(sketch, "E267", {"points": [v(92.23, -15.7) * mm, v(93.16, -15.8) * mm, v(93.86, -16.43) * mm, v(94.07, -17.36) * mm]});
            skFitSpline(sketch, "E268", {"points": [v(94.07, -17.36) * mm, v(94.2, -17.97) * mm, v(94.25, -18.59) * mm, v(94.3, -19.03) * mm]});
            skFitSpline(sketch, "E269", {"points": [v(94.3, -19.03) * mm, v(94.11, -22.34) * mm, v(93.11, -25.15) * mm, v(91.12, -27.57) * mm]});
            skFitSpline(sketch, "E270", {"points": [v(91.12, -27.57) * mm, v(90.52, -28.3) * mm, v(89.77, -28.86) * mm, v(88.82, -29.09) * mm]});
            skFitSpline(sketch, "E271", {"points": [v(88.82, -29.09) * mm, v(87.8, -29.33) * mm, v(86.89, -28.88) * mm, v(86.5, -27.9) * mm]});
            skFitSpline(sketch, "E272", {"points": [v(86.5, -27.9) * mm, v(86.03, -26.75) * mm, v(86.1, -25.55) * mm, v(86.28, -24.37) * mm]});
            skFitSpline(sketch, "E273", {"points": [v(86.28, -24.37) * mm, v(86.65, -22.05) * mm, v(87.43, -19.88) * mm, v(88.8, -17.95) * mm]});
            skFitSpline(sketch, "E274", {"points": [v(88.8, -17.95) * mm, v(89.22, -17.36) * mm, v(89.75, -16.82) * mm, v(90.3, -16.34) * mm]});
            skFitSpline(sketch, "E275", {"points": [v(90.3, -16.34) * mm, v(90.77, -15.93) * mm, v(91.33, -15.68) * mm, v(91.96, -15.68) * mm]});
            skFitSpline(sketch, "E276", {"points": [v(81.3, -6.22) * mm, v(80.37, -6.22) * mm, v(79.54, -7.05) * mm, v(79.57, -7.95) * mm]});
            skFitSpline(sketch, "E277", {"points": [v(79.57, -7.95) * mm, v(79.58, -8.65) * mm, v(80.16, -9.2) * mm, v(80.88, -9.2) * mm]});
            skFitSpline(sketch, "E278", {"points": [v(80.88, -9.2) * mm, v(81.76, -9.2) * mm, v(82.55, -8.39) * mm, v(82.54, -7.48) * mm]});
            skFitSpline(sketch, "E279", {"points": [v(82.54, -7.48) * mm, v(82.54, -6.72) * mm, v(82.04, -6.22) * mm, v(81.3, -6.22) * mm]});
            skFitSpline(sketch, "E280", {"points": [v(-31.53, -9.56) * mm, v(-31.75, -9.56) * mm, v(-31.95, -9.61) * mm, v(-32.06, -9.97) * mm]});
            skLineSegment(sketch, "E281", {"start": v(-32.06, -9.97) * mm, "end": v(-28.1, -9.97) * mm});
            skFitSpline(sketch, "E282", {"points": [v(-28.1, -9.97) * mm, v(-28.76, -10.54) * mm, v(-29.03, -11.2) * mm, v(-29.23, -11.89) * mm]});
            skFitSpline(sketch, "E283", {"points": [v(-29.23, -11.89) * mm, v(-29.87, -14.1) * mm, v(-30.48, -16.3) * mm, v(-31.1, -18.5) * mm]});
            skFitSpline(sketch, "E284", {"points": [v(-31.1, -18.5) * mm, v(-31.14, -18.62) * mm, v(-31.2, -18.72) * mm, v(-31.25, -18.83) * mm]});
            skFitSpline(sketch, "E285", {"points": [v(-31.25, -18.83) * mm, v(-31.34, -18.64) * mm, v(-31.33, -18.47) * mm, v(-31.36, -18.31) * mm]});
            skFitSpline(sketch, "E286", {"points": [v(-31.36, -18.31) * mm, v(-31.7, -16.85) * mm, v(-32.42, -16.01) * mm, v(-33.86, -16.01) * mm]});
            skFitSpline(sketch, "E287", {"points": [v(-33.86, -16.01) * mm, v(-34.85, -16.01) * mm, v(-35.8, -16.25) * mm, v(-36.68, -16.72) * mm]});
            skFitSpline(sketch, "E288", {"points": [v(-36.68, -16.72) * mm, v(-38.85, -17.88) * mm, v(-40.26, -19.7) * mm, v(-41.3, -21.86) * mm]});
            skFitSpline(sketch, "E289", {"points": [v(-41.3, -21.86) * mm, v(-41.97, -23.23) * mm, v(-42.35, -24.68) * mm, v(-42.28, -26.22) * mm]});
            skFitSpline(sketch, "E290", {"points": [v(-42.28, -26.22) * mm, v(-42.18, -28.52) * mm, v(-40.65, -30) * mm, v(-38.36, -30.03) * mm]});
            skFitSpline(sketch, "E291", {"points": [v(-38.36, -30.03) * mm, v(-37.85, -30.04) * mm, v(-37.37, -29.96) * mm, v(-36.9, -29.74) * mm]});
            skFitSpline(sketch, "E292", {"points": [v(-36.9, -29.74) * mm, v(-35.9, -29.28) * mm, v(-35.1, -28.59) * mm, v(-34.4, -27.75) * mm]});
            skFitSpline(sketch, "E293", {"points": [v(-34.4, -27.75) * mm, v(-34.09, -27.37) * mm, v(-33.8, -26.96) * mm, v(-33.41, -26.46) * mm]});
            skFitSpline(sketch, "E294", {"points": [v(-33.41, -26.46) * mm, v(-33.41, -26.82) * mm, v(-33.41, -27.05) * mm, v(-33.41, -27.27) * mm]});
            skFitSpline(sketch, "E295", {"points": [v(-33.41, -27.27) * mm, v(-33.42, -28.4) * mm, v(-32.85, -29.17) * mm, v(-31.85, -29.63) * mm]});
            skFitSpline(sketch, "E296", {"points": [v(-31.85, -29.63) * mm, v(-31.63, -29.72) * mm, v(-31.4, -29.82) * mm, v(-31.18, -29.88) * mm]});
            skFitSpline(sketch, "E297", {"points": [v(-31.18, -29.88) * mm, v(-30.37, -30.1) * mm, v(-29.64, -30.1) * mm, v(-28.96, -29.84) * mm]});
            skFitSpline(sketch, "E298", {"points": [v(-28.61, -29.7) * mm, v(-27.61, -29.22) * mm, v(-27.03, -28.31) * mm, v(-26.62, -27.25) * mm]});
            skFitSpline(sketch, "E299", {"points": [v(-26.62, -27.25) * mm, v(-26.49, -26.88) * mm, v(-26.44, -26.49) * mm, v(-26.32, -25.97) * mm]});
            skFitSpline(sketch, "E300", {"points": [v(-26.32, -25.97) * mm, v(-26.74, -26.34) * mm, v(-26.71, -26.35) * mm, v(-26.81, -26.7) * mm]});
            skFitSpline(sketch, "E301", {"points": [v(-26.81, -26.7) * mm, v(-27.14, -27.9) * mm, v(-27.7, -28.9) * mm, v(-28.82, -29.42) * mm]});
            skFitSpline(sketch, "E302", {"points": [v(-29.14, -29.57) * mm, v(-30.2, -29.98) * mm, v(-30.95, -29.53) * mm, v(-30.94, -28.42) * mm]});
            skFitSpline(sketch, "E303", {"points": [v(-30.94, -28.42) * mm, v(-30.93, -27.85) * mm, v(-30.85, -27.27) * mm, v(-30.7, -26.72) * mm]});
            skFitSpline(sketch, "E304", {"points": [v(-30.7, -26.72) * mm, v(-30.29, -25.17) * mm, v(-29.82, -23.64) * mm, v(-29.4, -22.1) * mm]});
            skFitSpline(sketch, "E305", {"points": [v(-29.4, -22.1) * mm, v(-28.46, -18.76) * mm, v(-27.54, -15.42) * mm, v(-26.61, -12.08) * mm]});
            skFitSpline(sketch, "E306", {"points": [v(-26.61, -12.08) * mm, v(-26.4, -11.31) * mm, v(-25.97, -9.62) * mm, v(-25.9, -9.56) * mm]});
            skFitSpline(sketch, "E307", {"points": [v(-25.9, -9.56) * mm, v(-26.48, -9.55) * mm, v(-30.96, -9.56) * mm, v(-31.53, -9.56) * mm]});
            skFitSpline(sketch, "E308", {"points": [v(-33.75, -16.36) * mm, v(-33.17, -16.38) * mm, v(-32.62, -16.61) * mm, v(-32.23, -17.06) * mm]});
            skFitSpline(sketch, "E309", {"points": [v(-32.23, -17.06) * mm, v(-31.86, -17.5) * mm, v(-31.72, -18.02) * mm, v(-31.67, -18.58) * mm]});
            skFitSpline(sketch, "E310", {"points": [v(-31.67, -18.58) * mm, v(-31.64, -18.86) * mm, v(-31.66, -19.15) * mm, v(-31.66, -19.44) * mm]});
            skFitSpline(sketch, "E311", {"points": [v(-31.66, -19.44) * mm, v(-31.63, -19.44) * mm, v(-31.59, -19.45) * mm, v(-31.55, -19.46) * mm]});
            skFitSpline(sketch, "E312", {"points": [v(-31.55, -19.46) * mm, v(-31.69, -20.15) * mm, v(-31.78, -20.86) * mm, v(-31.97, -21.54) * mm]});
            skFitSpline(sketch, "E313", {"points": [v(-31.97, -21.54) * mm, v(-32.32, -22.76) * mm, v(-32.63, -24) * mm, v(-33.14, -25.14) * mm]});
            skFitSpline(sketch, "E314", {"points": [v(-33.14, -25.14) * mm, v(-33.96, -26.96) * mm, v(-35.19, -28.47) * mm, v(-37.02, -29.4) * mm]});
            skFitSpline(sketch, "E315", {"points": [v(-37.02, -29.4) * mm, v(-37.19, -29.49) * mm, v(-37.37, -29.56) * mm, v(-37.55, -29.62) * mm]});
            skFitSpline(sketch, "E316", {"points": [v(-37.55, -29.62) * mm, v(-38.42, -29.88) * mm, v(-39.24, -29.48) * mm, v(-39.57, -28.63) * mm]});
            skFitSpline(sketch, "E317", {"points": [v(-39.57, -28.63) * mm, v(-39.96, -27.66) * mm, v(-39.92, -26.64) * mm, v(-39.76, -25.66) * mm]});
            skFitSpline(sketch, "E318", {"points": [v(-39.76, -25.66) * mm, v(-39.38, -23.25) * mm, v(-38.54, -21) * mm, v(-37.22, -18.93) * mm]});
            skFitSpline(sketch, "E319", {"points": [v(-37.22, -18.93) * mm, v(-36.75, -18.18) * mm, v(-36.16, -17.53) * mm, v(-35.47, -16.97) * mm]});
            skFitSpline(sketch, "E320", {"points": [v(-35.47, -16.97) * mm, v(-34.95, -16.55) * mm, v(-34.33, -16.35) * mm, v(-33.75, -16.36) * mm]});
            skFitSpline(sketch, "E321", {"points": [v(-15.97, -16.03) * mm, v(-16.45, -16.01) * mm, v(-16.92, -16.07) * mm, v(-17.4, -16.19) * mm]});
            skFitSpline(sketch, "E322", {"points": [v(-17.4, -16.19) * mm, v(-18.96, -16.57) * mm, v(-20.22, -17.49) * mm, v(-21.3, -18.63) * mm]});
            skFitSpline(sketch, "E323", {"points": [v(-21.3, -18.63) * mm, v(-22.23, -19.62) * mm, v(-23, -20.76) * mm, v(-23.54, -22.02) * mm]});
            skFitSpline(sketch, "E324", {"points": [v(-23.54, -22.02) * mm, v(-24.13, -23.4) * mm, v(-24.57, -24.8) * mm, v(-24.48, -26.33) * mm]});
            skFitSpline(sketch, "E325", {"points": [v(-24.48, -26.33) * mm, v(-24.35, -28.48) * mm, v(-22.98, -29.9) * mm, v(-20.7, -30.03) * mm]});
            skFitSpline(sketch, "E326", {"points": [v(-20.7, -30.03) * mm, v(-19.53, -30.1) * mm, v(-18.6, -29.6) * mm, v(-17.8, -28.86) * mm]});
            skFitSpline(sketch, "E327", {"points": [v(-17.8, -28.86) * mm, v(-17.15, -28.27) * mm, v(-16.62, -27.55) * mm, v(-16.04, -26.89) * mm]});
            skFitSpline(sketch, "E328", {"points": [v(-16.04, -26.89) * mm, v(-15.9, -26.74) * mm, v(-15.78, -26.58) * mm, v(-15.6, -26.37) * mm]});
            skFitSpline(sketch, "E329", {"points": [v(-15.6, -26.37) * mm, v(-15.6, -26.75) * mm, v(-15.61, -27.04) * mm, v(-15.6, -27.32) * mm]});
            skFitSpline(sketch, "E330", {"points": [v(-15.6, -27.32) * mm, v(-15.54, -28.07) * mm, v(-15.29, -28.73) * mm, v(-14.7, -29.22) * mm]});
            skFitSpline(sketch, "E331", {"points": [v(-14.7, -29.22) * mm, v(-13.62, -30.14) * mm, v(-11.48, -30.47) * mm, v(-10.16, -29.2) * mm]});
            skFitSpline(sketch, "E332", {"points": [v(-10.16, -29.2) * mm, v(-10.16, -29.2) * mm, v(-10.16, -29.2) * mm, v(-10.15, -29.2) * mm]});
            skFitSpline(sketch, "E333", {"points": [v(-10.15, -29.2) * mm, v(-9.6, -28.69) * mm, v(-9.22, -28) * mm, v(-8.93, -27.24) * mm]});
            skFitSpline(sketch, "E334", {"points": [v(-8.93, -27.24) * mm, v(-8.8, -26.88) * mm, v(-8.75, -26.48) * mm, v(-8.63, -25.96) * mm]});
            skFitSpline(sketch, "E335", {"points": [v(-8.63, -25.96) * mm, v(-9.05, -26.33) * mm, v(-9.03, -26.34) * mm, v(-9.12, -26.7) * mm]});
            skFitSpline(sketch, "E336", {"points": [v(-9.12, -26.7) * mm, v(-9.36, -27.59) * mm, v(-9.73, -28.36) * mm, v(-10.35, -28.92) * mm]});
            skFitSpline(sketch, "E337", {"points": [v(-10.35, -28.92) * mm, v(-10.5, -29.05) * mm, v(-10.66, -29.18) * mm, v(-10.84, -29.28) * mm]});
            skFitSpline(sketch, "E338", {"points": [v(-10.84, -29.28) * mm, v(-10.84, -29.28) * mm, v(-10.85, -29.28) * mm, v(-10.85, -29.28) * mm]});
            skFitSpline(sketch, "E339", {"points": [v(-10.85, -29.28) * mm, v(-11.05, -29.4) * mm, v(-11.27, -29.5) * mm, v(-11.5, -29.58) * mm]});
            skFitSpline(sketch, "E340", {"points": [v(-11.5, -29.58) * mm, v(-12.59, -29.96) * mm, v(-13.28, -29.5) * mm, v(-13.22, -28.35) * mm]});
            skFitSpline(sketch, "E341", {"points": [v(-13.22, -28.35) * mm, v(-13.2, -27.74) * mm, v(-13.02, -27.13) * mm, v(-12.85, -26.53) * mm]});
            skFitSpline(sketch, "E342", {"points": [v(-12.85, -26.53) * mm, v(-11.95, -23.26) * mm, v(-10.06, -16.41) * mm, v(-10.01, -16.15) * mm]});
            skFitSpline(sketch, "E343", {"points": [v(-10.01, -16.15) * mm, v(-10.9, -16.08) * mm, v(-11.71, -16.1) * mm, v(-12.5, -16.14) * mm]});
            skFitSpline(sketch, "E344", {"points": [v(-12.5, -16.14) * mm, v(-12.58, -16.26) * mm, v(-13.15, -17.9) * mm, v(-13.4, -18.69) * mm]});
            skFitSpline(sketch, "E345", {"points": [v(-13.4, -18.69) * mm, v(-13.6, -18.12) * mm, v(-13.75, -17.56) * mm, v(-14, -17.06) * mm]});
            skFitSpline(sketch, "E346", {"points": [v(-14, -17.06) * mm, v(-14.3, -16.5) * mm, v(-14.8, -16.15) * mm, v(-15.48, -16.06) * mm]});
            skFitSpline(sketch, "E347", {"points": [v(-15.48, -16.06) * mm, v(-15.65, -16.04) * mm, v(-15.8, -16.03) * mm, v(-15.97, -16.03) * mm]});
            skFitSpline(sketch, "E348", {"points": [v(-16, -16.38) * mm, v(-14.96, -16.37) * mm, v(-14.31, -16.82) * mm, v(-14.04, -17.81) * mm]});
            skFitSpline(sketch, "E349", {"points": [v(-14.04, -17.81) * mm, v(-13.72, -18.94) * mm, v(-13.78, -20.08) * mm, v(-14.1, -21.2) * mm]});
            skFitSpline(sketch, "E350", {"points": [v(-14.1, -21.2) * mm, v(-14.4, -22.28) * mm, v(-14.7, -23.37) * mm, v(-15.07, -24.42) * mm]});
            skFitSpline(sketch, "E351", {"points": [v(-15.07, -24.42) * mm, v(-15.65, -26.05) * mm, v(-16.63, -27.44) * mm, v(-17.96, -28.54) * mm]});
            skFitSpline(sketch, "E352", {"points": [v(-17.96, -28.54) * mm, v(-18.43, -28.93) * mm, v(-19, -29.2) * mm, v(-19.53, -29.51) * mm]});
            skFitSpline(sketch, "E353", {"points": [v(-19.53, -29.51) * mm, v(-20.46, -30.05) * mm, v(-21.77, -29.6) * mm, v(-22, -28.03) * mm]});
            skFitSpline(sketch, "E354", {"points": [v(-22, -28.03) * mm, v(-22.06, -27.65) * mm, v(-22, -27.26) * mm, v(-22, -26.88) * mm]});
            skFitSpline(sketch, "E355", {"points": [v(-22, -26.88) * mm, v(-22.1, -25.34) * mm, v(-21.63, -23.9) * mm, v(-21.14, -22.49) * mm]});
            skFitSpline(sketch, "E356", {"points": [v(-21.14, -22.49) * mm, v(-20.5, -20.7) * mm, v(-19.65, -19.01) * mm, v(-18.33, -17.62) * mm]});
            skFitSpline(sketch, "E357", {"points": [v(-18.33, -17.62) * mm, v(-17.7, -16.95) * mm, v(-16.99, -16.4) * mm, v(-16, -16.38) * mm]});
            skFitSpline(sketch, "E358", {"points": [v(37.64, -10.66) * mm, v(37.27, -11.14) * mm, v(37.03, -11.55) * mm, v(36.7, -11.88) * mm]});
            skFitSpline(sketch, "E359", {"points": [v(36.7, -11.88) * mm, v(36.35, -12.2) * mm, v(35.93, -12.45) * mm, v(35.53, -12.72) * mm]});
            skFitSpline(sketch, "E360", {"points": [v(35.53, -12.72) * mm, v(34.81, -13.23) * mm, v(34.24, -13.85) * mm, v(33.95, -14.7) * mm]});
            skFitSpline(sketch, "E361", {"points": [v(33.95, -14.7) * mm, v(33.85, -15.01) * mm, v(33.7, -15.31) * mm, v(33.58, -15.62) * mm]});
            skFitSpline(sketch, "E362", {"points": [v(33.58, -15.62) * mm, v(32.98, -15.62) * mm, v(32.52, -15.62) * mm, v(32.36, -15.62) * mm]});
            skFitSpline(sketch, "E363", {"points": [v(32.36, -15.62) * mm, v(32.14, -15.61) * mm, v(31.94, -15.67) * mm, v(31.83, -16.03) * mm]});
            skFitSpline(sketch, "E364", {"points": [v(31.83, -16.03) * mm, v(32.35, -16.03) * mm, v(33.41, -16.05) * mm, v(33.47, -16.06) * mm]});
            skFitSpline(sketch, "E365", {"points": [v(33.47, -16.06) * mm, v(33.42, -16.28) * mm, v(33.4, -16.46) * mm, v(33.34, -16.64) * mm]});
            skFitSpline(sketch, "E366", {"points": [v(33.34, -16.64) * mm, v(32.75, -18.7) * mm, v(32.15, -20.77) * mm, v(31.56, -22.84) * mm]});
            skFitSpline(sketch, "E367", {"points": [v(31.56, -22.84) * mm, v(31.26, -23.9) * mm, v(30.95, -24.95) * mm, v(30.69, -26.02) * mm]});
            skFitSpline(sketch, "E368", {"points": [v(30.69, -26.02) * mm, v(30.4, -27.22) * mm, v(30.8, -28.27) * mm, v(31.86, -28.85) * mm]});
            skFitSpline(sketch, "E369", {"points": [v(31.86, -28.85) * mm, v(33.82, -29.92) * mm, v(35.84, -29.49) * mm, v(36.9, -27.63) * mm]});
            skFitSpline(sketch, "E370", {"points": [v(37.45, -26) * mm, v(37.09, -26.3) * mm, v(37.11, -26.3) * mm, v(37.02, -26.61) * mm]});
            skFitSpline(sketch, "E371", {"points": [v(37.02, -26.61) * mm, v(36.93, -26.94) * mm, v(36.8, -27.24) * mm, v(36.66, -27.53) * mm]});
            skFitSpline(sketch, "E372", {"points": [v(36.66, -27.53) * mm, v(36.16, -28.3) * mm, v(35.5, -28.88) * mm, v(34.49, -29.12) * mm]});
            skFitSpline(sketch, "E373", {"points": [v(34.49, -29.12) * mm, v(33.65, -29.32) * mm, v(33.03, -28.89) * mm, v(33.03, -28.02) * mm]});
            skFitSpline(sketch, "E374", {"points": [v(33.03, -28.02) * mm, v(33.02, -27.46) * mm, v(33.1, -26.87) * mm, v(33.25, -26.33) * mm]});
            skFitSpline(sketch, "E375", {"points": [v(33.25, -26.33) * mm, v(34.04, -23.5) * mm, v(34.86, -20.68) * mm, v(35.68, -17.85) * mm]});
            skFitSpline(sketch, "E376", {"points": [v(35.68, -17.85) * mm, v(35.85, -17.26) * mm, v(36.05, -16.67) * mm, v(36.25, -16.03) * mm]});
            skLineSegment(sketch, "E377", {"start": v(36.25, -16.03) * mm, "end": v(39.3, -16.03) * mm});
            skFitSpline(sketch, "E378", {"points": [v(39.3, -16.03) * mm, v(39.44, -15.9) * mm, v(39.43, -15.76) * mm, v(39.57, -15.63) * mm]});
            skFitSpline(sketch, "E379", {"points": [v(39.57, -15.63) * mm, v(39.25, -15.62) * mm, v(37.73, -15.62) * mm, v(36.34, -15.62) * mm]});
            skFitSpline(sketch, "E380", {"points": [v(36.34, -15.62) * mm, v(36.48, -15.12) * mm, v(36.6, -14.73) * mm, v(36.71, -14.34) * mm]});
            skFitSpline(sketch, "E381", {"points": [v(36.71, -14.34) * mm, v(36.82, -13.95) * mm, v(36.93, -13.55) * mm, v(37.04, -13.16) * mm]});
            skFitSpline(sketch, "E382", {"points": [v(37.04, -13.16) * mm, v(37.16, -12.75) * mm, v(37.3, -12.34) * mm, v(37.4, -11.92) * mm]});
            skFitSpline(sketch, "E383", {"points": [v(37.4, -11.92) * mm, v(37.5, -11.54) * mm, v(37.7, -11.17) * mm, v(37.64, -10.66) * mm]});
            skFitSpline(sketch, "E384", {"points": [v(41.3, -15.61) * mm, v(41.09, -15.61) * mm, v(40.88, -15.67) * mm, v(40.77, -16.03) * mm]});
            skLineSegment(sketch, "E385", {"start": v(40.77, -16.03) * mm, "end": v(43.84, -16.03) * mm});
            skFitSpline(sketch, "E386", {"points": [v(43.84, -16.03) * mm, v(43.03, -16.51) * mm, v(42.48, -17.14) * mm, v(42.22, -18.01) * mm]});
            skFitSpline(sketch, "E387", {"points": [v(42.22, -18.01) * mm, v(41.47, -20.53) * mm, v(40.73, -23.05) * mm, v(40, -25.58) * mm]});
            skFitSpline(sketch, "E388", {"points": [v(40, -25.58) * mm, v(39.82, -26.2) * mm, v(39.8, -26.86) * mm, v(40, -27.49) * mm]});
            skFitSpline(sketch, "E389", {"points": [v(40, -27.49) * mm, v(40.48, -28.95) * mm, v(42.13, -29.75) * mm, v(43.74, -29.33) * mm]});
            skFitSpline(sketch, "E390", {"points": [v(43.74, -29.33) * mm, v(45.13, -28.97) * mm, v(46.14, -28.08) * mm, v(47.04, -27.02) * mm]});
            skFitSpline(sketch, "E391", {"points": [v(47.04, -27.02) * mm, v(47.38, -26.6) * mm, v(47.7, -26.16) * mm, v(48.13, -25.6) * mm]});
            skFitSpline(sketch, "E392", {"points": [v(48.13, -25.6) * mm, v(48.07, -25.95) * mm, v(48.04, -26.13) * mm, v(48.01, -26.32) * mm]});
            skFitSpline(sketch, "E393", {"points": [v(48.01, -26.32) * mm, v(47.9, -27.12) * mm, v(48.1, -27.84) * mm, v(48.66, -28.43) * mm]});
            skFitSpline(sketch, "E394", {"points": [v(48.66, -28.43) * mm, v(50.12, -29.95) * mm, v(52.82, -29.76) * mm, v(54.04, -28.06) * mm]});
            skFitSpline(sketch, "E395", {"points": [v(54.04, -28.06) * mm, v(54.24, -27.78) * mm, v(54.4, -27.49) * mm, v(54.54, -27.19) * mm]});
            skFitSpline(sketch, "E396", {"points": [v(54.87, -25.97) * mm, v(54.48, -26.3) * mm, v(54.48, -26.3) * mm, v(54.4, -26.64) * mm]});
            skFitSpline(sketch, "E397", {"points": [v(54.4, -26.64) * mm, v(54.33, -27) * mm, v(54.2, -27.2) * mm, v(54.08, -27.47) * mm]});
            skFitSpline(sketch, "E398", {"points": [v(54.08, -27.47) * mm, v(53.9, -27.76) * mm, v(53.7, -28.03) * mm, v(53.47, -28.27) * mm]});
            skFitSpline(sketch, "E399", {"points": [v(53.47, -28.27) * mm, v(52.96, -28.8) * mm, v(52.36, -29.18) * mm, v(51.58, -29.18) * mm]});
            skFitSpline(sketch, "E400", {"points": [v(51.58, -29.18) * mm, v(50.88, -29.19) * mm, v(50.49, -28.88) * mm, v(50.43, -28.19) * mm]});
            skFitSpline(sketch, "E401", {"points": [v(50.43, -28.19) * mm, v(50.4, -27.74) * mm, v(50.41, -27.27) * mm, v(50.53, -26.84) * mm]});
            skFitSpline(sketch, "E402", {"points": [v(50.53, -26.84) * mm, v(51.33, -23.94) * mm, v(52.17, -21.04) * mm, v(53, -18.15) * mm]});
            skFitSpline(sketch, "E403", {"points": [v(53, -18.15) * mm, v(53.21, -17.37) * mm, v(53.43, -16.6) * mm, v(53.67, -15.71) * mm]});
            skFitSpline(sketch, "E404", {"points": [v(53.67, -15.71) * mm, v(52.73, -15.65) * mm, v(51.92, -15.64) * mm, v(51.1, -15.71) * mm]});
            skFitSpline(sketch, "E405", {"points": [v(51.1, -15.71) * mm, v(51.01, -15.92) * mm, v(49.77, -20.03) * mm, v(49.24, -21.94) * mm]});
            skFitSpline(sketch, "E406", {"points": [v(49.24, -21.94) * mm, v(48.6, -24.28) * mm, v(47.54, -26.36) * mm, v(45.7, -27.98) * mm]});
            skFitSpline(sketch, "E407", {"points": [v(45.7, -27.98) * mm, v(45.08, -28.53) * mm, v(44.37, -28.93) * mm, v(43.57, -29.11) * mm]});
            skFitSpline(sketch, "E408", {"points": [v(43.57, -29.11) * mm, v(43.02, -29.24) * mm, v(42.42, -29.36) * mm, v(41.94, -28.66) * mm]});
            skFitSpline(sketch, "E409", {"points": [v(41.94, -28.66) * mm, v(41.85, -28.38) * mm, v(41.97, -27.99) * mm, v(42.07, -27.63) * mm]});
            skFitSpline(sketch, "E410", {"points": [v(42.07, -27.63) * mm, v(43.13, -23.93) * mm, v(45.46, -15.65) * mm, v(45.48, -15.62) * mm]});
            skFitSpline(sketch, "E411", {"points": [v(45.48, -15.62) * mm, v(44.57, -15.62) * mm, v(41.52, -15.61) * mm, v(41.3, -15.61) * mm]});
            skFitSpline(sketch, "E412", {"points": [v(67.37, -8.98) * mm, v(67.15, -8.98) * mm, v(66.95, -9.04) * mm, v(66.83, -9.4) * mm]});
            skLineSegment(sketch, "E413", {"start": v(66.83, -9.4) * mm, "end": v(70.76, -9.4) * mm});
            skFitSpline(sketch, "E414", {"points": [v(70.76, -9.4) * mm, v(70.04, -10.06) * mm, v(69.75, -10.81) * mm, v(69.53, -11.59) * mm]});
            skFitSpline(sketch, "E415", {"points": [v(69.53, -11.59) * mm, v(69, -13.5) * mm, v(68.46, -15.4) * mm, v(67.92, -17.31) * mm]});
            skFitSpline(sketch, "E416", {"points": [v(67.92, -17.31) * mm, v(67.82, -17.7) * mm, v(67.7, -18.06) * mm, v(67.58, -18.44) * mm]});
            skFitSpline(sketch, "E417", {"points": [v(67.58, -18.44) * mm, v(67.43, -18.23) * mm, v(67.42, -18.05) * mm, v(67.4, -17.87) * mm]});
            skFitSpline(sketch, "E418", {"points": [v(67.4, -17.87) * mm, v(67.26, -16.4) * mm, v(66.3, -15.54) * mm, v(64.84, -15.53) * mm]});
            skFitSpline(sketch, "E419", {"points": [v(64.84, -15.53) * mm, v(63.22, -15.52) * mm, v(61.87, -16.2) * mm, v(60.67, -17.2) * mm]});
            skFitSpline(sketch, "E420", {"points": [v(60.67, -17.2) * mm, v(58.73, -18.8) * mm, v(57.5, -20.88) * mm, v(56.81, -23.29) * mm]});
            skFitSpline(sketch, "E421", {"points": [v(56.81, -23.29) * mm, v(56.54, -24.25) * mm, v(56.5, -25.23) * mm, v(56.61, -26.21) * mm]});
            skFitSpline(sketch, "E422", {"points": [v(56.61, -26.21) * mm, v(56.7, -27.03) * mm, v(57.04, -27.78) * mm, v(57.64, -28.37) * mm]});
            skFitSpline(sketch, "E423", {"points": [v(57.64, -28.37) * mm, v(58.85, -29.58) * mm, v(60.94, -29.82) * mm, v(62.42, -28.91) * mm]});
            skFitSpline(sketch, "E424", {"points": [v(62.42, -28.91) * mm, v(63.46, -28.28) * mm, v(64.28, -27.41) * mm, v(64.97, -26.42) * mm]});
            skFitSpline(sketch, "E425", {"points": [v(64.97, -26.42) * mm, v(65.08, -26.27) * mm, v(65.21, -26.12) * mm, v(65.34, -25.97) * mm]});
            skFitSpline(sketch, "E426", {"points": [v(65.34, -25.97) * mm, v(65.42, -26.2) * mm, v(65.4, -26.36) * mm, v(65.4, -26.52) * mm]});
            skFitSpline(sketch, "E427", {"points": [v(65.4, -26.52) * mm, v(65.36, -27.45) * mm, v(65.69, -28.22) * mm, v(66.44, -28.76) * mm]});
            skFitSpline(sketch, "E428", {"points": [v(66.44, -28.76) * mm, v(67.44, -29.47) * mm, v(68.58, -29.64) * mm, v(69.73, -29.31) * mm]});
            skFitSpline(sketch, "E429", {"points": [v(69.73, -29.31) * mm, v(70.74, -29.02) * mm, v(71.65, -28) * mm, v(72.06, -26.85) * mm]});
            skFitSpline(sketch, "E430", {"points": [v(71.91, -26.48) * mm, v(71.7, -27.09) * mm, v(71.42, -27.66) * mm, v(71, -28.14) * mm]});
            skFitSpline(sketch, "E431", {"points": [v(71, -28.14) * mm, v(70.43, -28.77) * mm, v(69.77, -29.21) * mm, v(68.88, -29.18) * mm]});
            skFitSpline(sketch, "E432", {"points": [v(68.88, -29.18) * mm, v(68.33, -29.16) * mm, v(68, -28.95) * mm, v(67.9, -28.4) * mm]});
            skFitSpline(sketch, "E433", {"points": [v(67.9, -28.4) * mm, v(67.83, -27.97) * mm, v(67.8, -27.49) * mm, v(67.9, -27.06) * mm]});
            skFitSpline(sketch, "E434", {"points": [v(67.9, -27.06) * mm, v(68.25, -25.55) * mm, v(68.66, -24.06) * mm, v(69.08, -22.56) * mm]});
            skFitSpline(sketch, "E435", {"points": [v(69.08, -22.56) * mm, v(70, -19.27) * mm, v(72.9, -9.13) * mm, v(73.04, -9) * mm]});
            skFitSpline(sketch, "E436", {"points": [v(73.04, -9) * mm, v(72.47, -9) * mm, v(67.94, -8.99) * mm, v(67.37, -8.98) * mm]});
            skFitSpline(sketch, "E437", {"points": [v(65.09, -15.82) * mm, v(66.25, -15.81) * mm, v(66.94, -16.54) * mm, v(67.2, -17.99) * mm]});
            skFitSpline(sketch, "E438", {"points": [v(67.2, -17.99) * mm, v(67.24, -18.29) * mm, v(67.2, -18.6) * mm, v(67.2, -18.92) * mm]});
            skFitSpline(sketch, "E439", {"points": [v(67.2, -18.92) * mm, v(67.28, -20.32) * mm, v(66.65, -21.56) * mm, v(66.33, -22.88) * mm]});
            skFitSpline(sketch, "E440", {"points": [v(66.33, -22.88) * mm, v(65.91, -24.65) * mm, v(65, -26.14) * mm, v(63.76, -27.45) * mm]});
            skFitSpline(sketch, "E441", {"points": [v(63.76, -27.45) * mm, v(63.15, -28.1) * mm, v(62.45, -28.63) * mm, v(61.63, -29) * mm]});
            skFitSpline(sketch, "E442", {"points": [v(61.63, -29) * mm, v(60.46, -29.5) * mm, v(59.48, -29.04) * mm, v(59.12, -27.81) * mm]});
            skFitSpline(sketch, "E443", {"points": [v(59.12, -27.81) * mm, v(58.83, -26.84) * mm, v(58.91, -25.86) * mm, v(59.07, -24.9) * mm]});
            skFitSpline(sketch, "E444", {"points": [v(59.07, -24.9) * mm, v(59.44, -22.58) * mm, v(60.25, -20.41) * mm, v(61.54, -18.45) * mm]});
            skFitSpline(sketch, "E445", {"points": [v(61.54, -18.45) * mm, v(62.01, -17.74) * mm, v(62.6, -17.1) * mm, v(63.23, -16.52) * mm]});
            skFitSpline(sketch, "E446", {"points": [v(63.23, -16.52) * mm, v(63.58, -16.2) * mm, v(64.09, -15.95) * mm, v(64.56, -15.87) * mm]});
            skFitSpline(sketch, "E447", {"points": [v(64.56, -15.87) * mm, v(64.74, -15.84) * mm, v(64.92, -15.82) * mm, v(65.09, -15.82) * mm]});
            skFitSpline(sketch, "E448", {"points": [v(81.45, -25.97) * mm, v(81.2, -26.18) * mm, v(81.14, -26.24) * mm, v(81.1, -26.38) * mm]});
            skLineSegment(sketch, "E449", {"start": v(81.1, -26.38) * mm, "end": v(81.1, -26.38) * mm});
            skFitSpline(sketch, "E450", {"points": [v(81.1, -26.38) * mm, v(80.68, -27.65) * mm, v(80, -28.7) * mm, v(78.59, -29.08) * mm]});
            skFitSpline(sketch, "E451", {"points": [v(78.59, -29.08) * mm, v(77.53, -29.38) * mm, v(76.93, -28.94) * mm, v(76.99, -27.84) * mm]});
            skFitSpline(sketch, "E452", {"points": [v(76.99, -27.84) * mm, v(77.02, -27.16) * mm, v(77.17, -26.47) * mm, v(77.36, -25.8) * mm]});
            skFitSpline(sketch, "E453", {"points": [v(77.36, -25.8) * mm, v(78.24, -22.68) * mm, v(80.2, -15.7) * mm, v(80.24, -15.67) * mm]});
            skFitSpline(sketch, "E454", {"points": [v(80.24, -15.67) * mm, v(79.66, -15.66) * mm, v(76.58, -15.66) * mm, v(76, -15.66) * mm]});
            skFitSpline(sketch, "E455", {"points": [v(76, -15.66) * mm, v(75.79, -15.66) * mm, v(75.58, -15.71) * mm, v(75.47, -16.07) * mm]});
            skLineSegment(sketch, "E456", {"start": v(75.47, -16.07) * mm, "end": v(78.58, -16.07) * mm});
            skFitSpline(sketch, "E457", {"points": [v(78.58, -16.07) * mm, v(77.52, -16.62) * mm, v(77.05, -17.58) * mm, v(76.75, -18.67) * mm]});
            skFitSpline(sketch, "E458", {"points": [v(76.75, -18.67) * mm, v(76.46, -19.7) * mm, v(76.16, -20.74) * mm, v(75.86, -21.77) * mm]});
            skFitSpline(sketch, "E459", {"points": [v(75.86, -21.77) * mm, v(75.45, -23.22) * mm, v(75, -24.66) * mm, v(74.63, -26.12) * mm]});
            skFitSpline(sketch, "E460", {"points": [v(74.63, -26.12) * mm, v(74.37, -27.13) * mm, v(74.69, -28) * mm, v(75.5, -28.68) * mm]});
            skFitSpline(sketch, "E461", {"points": [v(75.5, -28.68) * mm, v(76.5, -29.5) * mm, v(78.37, -29.7) * mm, v(79.45, -29.03) * mm]});
            skFitSpline(sketch, "E462", {"points": [v(79.45, -29.03) * mm, v(80.36, -28.46) * mm, v(80.95, -27.7) * mm, v(81.26, -26.73) * mm]});
            skLineSegment(sketch, "E463", {"start": v(-29.14, -29.57) * mm, "end": v(-28.82, -29.42) * mm});
            skLineSegment(sketch, "E464", {"start": v(-28.96, -29.84) * mm, "end": v(-28.61, -29.7) * mm});
            skLineSegment(sketch, "E465", {"start": v(36.9, -27.63) * mm, "end": v(37.48, -26.35) * mm});
            skLineSegment(sketch, "E466", {"start": v(37.48, -26.35) * mm, "end": v(37.45, -26) * mm});
            skLineSegment(sketch, "E467", {"start": v(54.54, -27.19) * mm, "end": v(54.73, -26.64) * mm});
            skLineSegment(sketch, "E468", {"start": v(54.73, -26.64) * mm, "end": v(54.81, -26.32) * mm});
            skLineSegment(sketch, "E469", {"start": v(54.81, -26.32) * mm, "end": v(54.87, -25.97) * mm});
            skLineSegment(sketch, "E470", {"start": v(71.91, -26.48) * mm, "end": v(71.97, -26.34) * mm});
            skLineSegment(sketch, "E471", {"start": v(71.97, -26.34) * mm, "end": v(72.04, -26.22) * mm});
            skLineSegment(sketch, "E472", {"start": v(72.04, -26.22) * mm, "end": v(72.12, -26.13) * mm});
            skLineSegment(sketch, "E473", {"start": v(72.12, -26.13) * mm, "end": v(72.27, -26.02) * mm});
            skLineSegment(sketch, "E474", {"start": v(72.06, -26.85) * mm, "end": v(72.27, -26.02) * mm});
            skLineSegment(sketch, "E475", {"start": v(81.45, -25.97) * mm, "end": v(81.26, -26.73) * mm});
            skSolve(sketch);
        }
        {
            var Q0;
            Q0=qSketchRegion(id+"F0",true);
            extrude(context, id + "F1", {"entities" : qUnion([Q0]), "depth" : 50 * mm, "offsetDistance" : 25 * mm});
        }
    });
